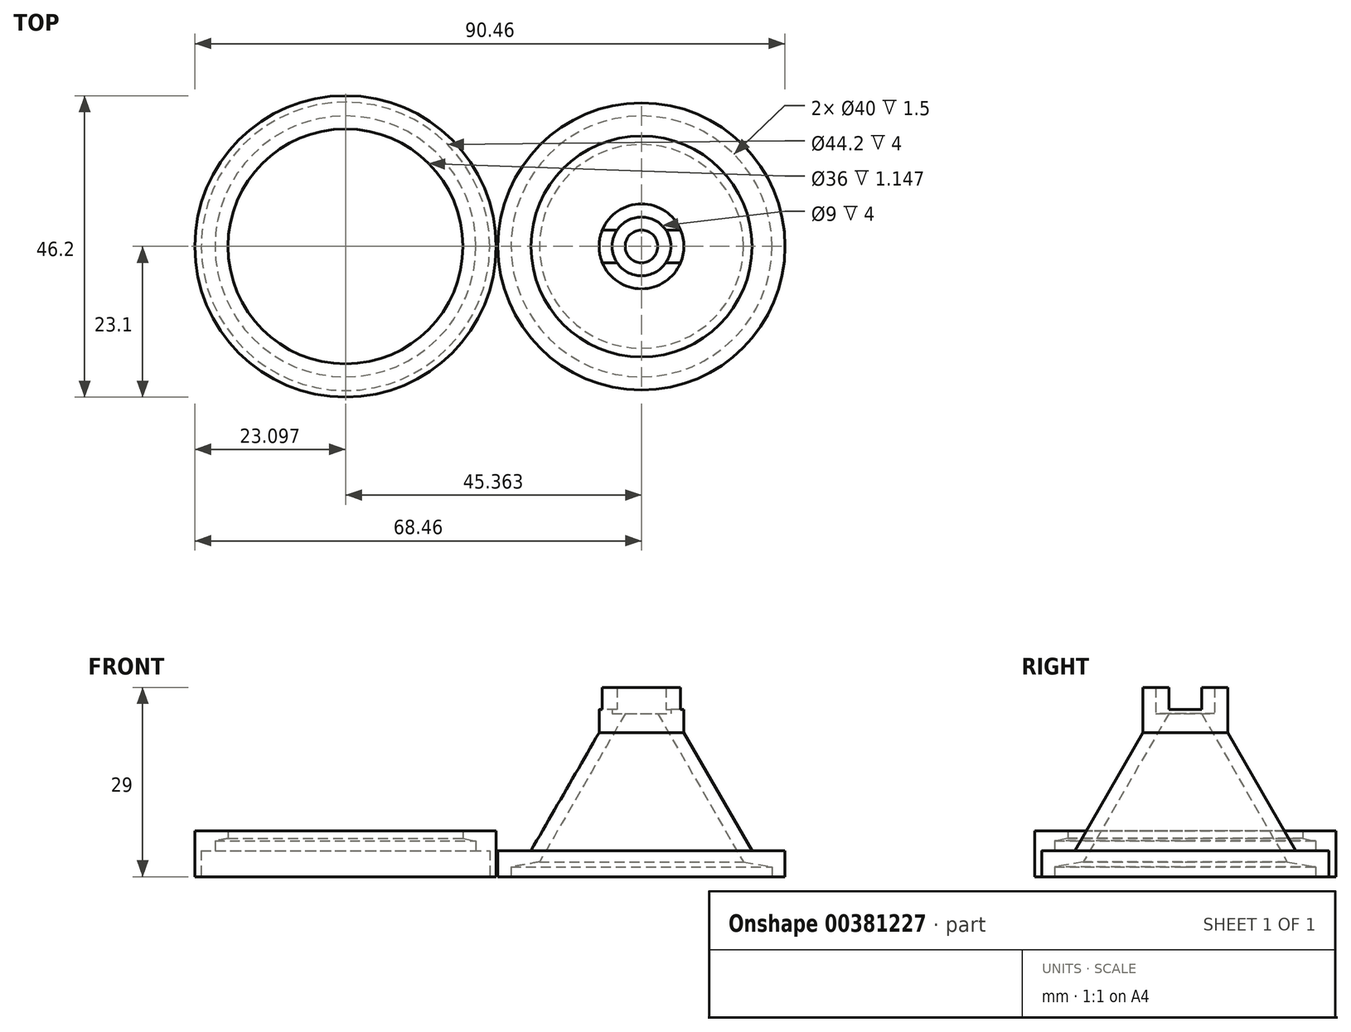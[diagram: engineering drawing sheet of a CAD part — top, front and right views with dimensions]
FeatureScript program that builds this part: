
annotation { "Feature Type Name" : "Feature", "Feature Type Description" : "" }
export const myFeature = defineFeature(function(context is Context, id is Id, definition is map)
    precondition{}
    {
        {
            var Q0;
            Q0=qCreatedBy(makeId("Front.planeOp"),FACE);
            var sketch = newSketch(context, id + "F0", { "sketchPlane" : qUnion([Q0])});
            skLineSegment(sketch, "E0", {"start": v(-20, 0) * mm, "end": v(-22, 0) * mm});
            skLineSegment(sketch, "E1", {"start": v(-22, 0) * mm, "end": v(-22, 4) * mm});
            skLineSegment(sketch, "E2", {"start": v(-22, 4) * mm, "end": v(-16.93, 4) * mm});
            skLineSegment(sketch, "E3", {"start": v(-16.93, 4) * mm, "end": v(-6.5, 22.07) * mm});
            skLineSegment(sketch, "E4", {"start": v(-6.5, 22.07) * mm, "end": v(-6.5, 29) * mm});
            skLineSegment(sketch, "E5", {"start": v(-6.5, 29) * mm, "end": v(-4.5, 29) * mm});
            skLineSegment(sketch, "E6", {"start": v(-4.5, 29) * mm, "end": v(-4.5, 25) * mm});
            skLineSegment(sketch, "E7", {"start": v(-4.5, 25) * mm, "end": v(-2.5, 25) * mm});
            skLineSegment(sketch, "E8", {"start": v(-2.5, 25) * mm, "end": v(-15.62, 2.27) * mm});
            skLineSegment(sketch, "E9", {"start": v(-15.62, 2.27) * mm, "end": v(-20, 1.5) * mm});
            skLineSegment(sketch, "E10", {"start": v(-20, 1.5) * mm, "end": v(-20, 0) * mm});
            skLineSegment(sketch, "E11", {"start": v(0, 0) * mm, "end": v(0, 30.95) * mm, "construction": true});
            skPoint(sketch, "E12.endSnap0", {"position": v(-22, 0) * mm});
            skSolve(sketch);
        }
        {
            var Q0;
            Q0=makeQuery(id+"F0.imprint","IMPRINT",FACE,{"disambiguationData":[TD([[makeQuery(id+"F0.imprint","IMPRINT",EDGE,{"derivedFrom":sQuery(id+"F0.wireOp",EDGE,"E0")}),-1.0]])]});
            var Q1;
            Q1=sQuery(id+"F0.wireOp",EDGE,"E11");
            revolve(context, id + "F1", {"entities" : qUnion([Q0]), "axis" : qUnion([Q1]), "revolveType" : RevolveType.FULL});
        }
        {
            var Q0;
            Q0=qCreatedBy(makeId("Right.planeOp"),FACE);
            var sketch = newSketch(context, id + "F2", { "sketchPlane" : qUnion([Q0])});
            skLineSegment(sketch, "E13.bottom", {"start": v(-2.5, 33.6) * mm, "end": v(2.5, 33.6) * mm});
            skLineSegment(sketch, "E13.top", {"start": v(-2.5, 25.6) * mm, "end": v(2.5, 25.6) * mm});
            skLineSegment(sketch, "E13.left", {"start": v(-2.5, 33.6) * mm, "end": v(-2.5, 25.6) * mm});
            skLineSegment(sketch, "E13.right", {"start": v(2.5, 33.6) * mm, "end": v(2.5, 25.6) * mm});
            skSolve(sketch);
        }
        {
            var Q0;
            Q0=makeQuery(id+"F2.imprint","IMPRINT",FACE,{"disambiguationData":[TD([[makeQuery(id+"F2.imprint","IMPRINT",EDGE,{"derivedFrom":sQuery(id+"F2.wireOp",EDGE,"E13.bottom")}),-1.0]])]});
            extrude(context, id + "F3", {"entities" : qUnion([Q0]), "operationType" : NewBodyOperationType.REMOVE, "endBound" : BoundingType.SYMMETRIC, "depth" : 15 * mm});
        }
        {
            var Q0;
            Q0=qCreatedBy(makeId("Front.planeOp"),FACE);
            var sketch = newSketch(context, id + "F4", { "sketchPlane" : qUnion([Q0])});
            skLineSegment(sketch, "E14", {"start": v(-68.46, 7) * mm, "end": v(-63.36, 7) * mm});
            skLineSegment(sketch, "E15", {"start": v(-63.36, 7) * mm, "end": v(-63.36, 5.85) * mm});
            skLineSegment(sketch, "E16", {"start": v(-63.36, 5.85) * mm, "end": v(-65.36, 5.5) * mm});
            skLineSegment(sketch, "E17", {"start": v(-65.36, 5.5) * mm, "end": v(-65.36, 4) * mm});
            skLineSegment(sketch, "E18", {"start": v(-45.36, 0.4) * mm, "end": v(-45.36, 15.1) * mm, "construction": true});
            skLineSegment(sketch, "E19", {"start": v(-65.36, 4) * mm, "end": v(-67.46, 4) * mm});
            skLineSegment(sketch, "E20", {"start": v(-67.46, 4) * mm, "end": v(-67.46, 0) * mm});
            skLineSegment(sketch, "E21", {"start": v(-68.46, 0) * mm, "end": v(-68.46, 7) * mm});
            skLineSegment(sketch, "E22", {"start": v(-68.46, 0) * mm, "end": v(-67.46, 0) * mm});
            skSolve(sketch);
        }
        {
            var Q0;
            Q0=makeQuery(id+"F4.imprint","IMPRINT",FACE,{"disambiguationData":[TD([[makeQuery(id+"F4.imprint","IMPRINT",EDGE,{"derivedFrom":sQuery(id+"F4.wireOp",EDGE,"E14")}),-1.0]])]});
            var Q1;
            Q1=sQuery(id+"F4.wireOp",EDGE,"E18");
            revolve(context, id + "F5", {"entities" : qUnion([Q0]), "axis" : qUnion([Q1]), "revolveType" : RevolveType.FULL});
        }
    });
